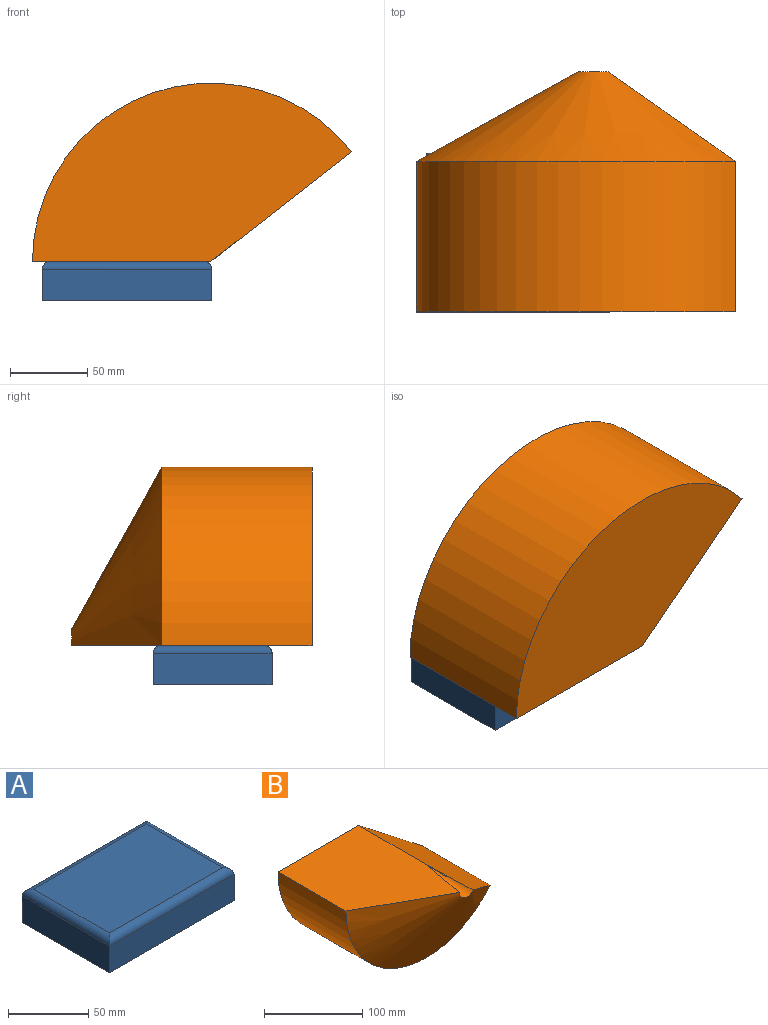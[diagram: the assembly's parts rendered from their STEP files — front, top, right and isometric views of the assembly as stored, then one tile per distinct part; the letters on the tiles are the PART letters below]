
ASSEMBLY  parts=2 mates=1
PART A: 10 faces, bbox 110x76.9x25.4 mm
  f0: plane 109.96x20.32mm, normal (0,1,0), area 2234.5mm2, adj f1,f3,f5,f6
  f1: plane 76.95x20.32mm, normal (-1,0,0), area 1563.6mm2, adj f0,f2,f5,f7
  f2: plane 109.96x20.32mm, normal (0,-1,0), area 2234.5mm2, adj f1,f3,f5,f9
  f3: plane 76.95x20.32mm, normal (1,0,0), area 1563.6mm2, adj f0,f2,f5,f8
  f4: plane 99.8x66.79mm, normal (0,0,1), area 6665.8mm2, adj f6,f7,f8,f9
  f5: plane 109.96x76.95mm, normal (0,0,-1), area 8461.6mm2, adj f0,f1,f2,f3
  f6: cylinder r=5.08mm len=109.96mm, axis (1,0,0), area 848mm2, adj f0,f4,f7,f8
  f7: cylinder r=5.08mm len=76.95mm, axis (0,1,0), area 584.6mm2, adj f1,f4,f6,f9
  f8: cylinder r=5.08mm len=76.95mm, axis (0,-1,0), area 584.6mm2, adj f3,f4,f6,f9
  f9: cylinder r=5.08mm len=109.96mm, axis (-1,0,0), area 848mm2, adj f2,f4,f7,f8
PART B: 6 faces, bbox 206.9x155.6x115.7 mm
  f0: plane 206.92x115.69mm, normal (0,1,0), area 16591.8mm2, adj f1,f4,f5
  f1: cylinder r=115.69mm len=206.92mm, axis (0,1,0), area 27975.2mm2, adj f0,f2,f4,f5
  f2: cone r=11.13mm half-angle=60.9deg, axis (0,1,0), area 18805.3mm2, adj f1,f3,f4,f5
  f3: cone r=0mm half-angle=10.8deg, axis (0,-1,0), area 815.8mm2, adj f2,f4,f5
  f4: plane 155.63x91.23mm, normal (0.62,0,0.79), area 14644.8mm2, adj f0,f1,f2,f3,f5
  f5: plane 155.63x115.69mm, normal (0,0,1), area 14644.8mm2, adj f0,f1,f2,f3,f4
PLACE A t=(0.93,-25.3,20.02)mm
PLACE B rot(axis=(1,0,0),180deg) t=(-22.54,-74.49,45.42)mm
MATE fastened B.f5 <-> A.f4  axis (0,0,-1) through (-76.82,-22.54,45.42)mm
